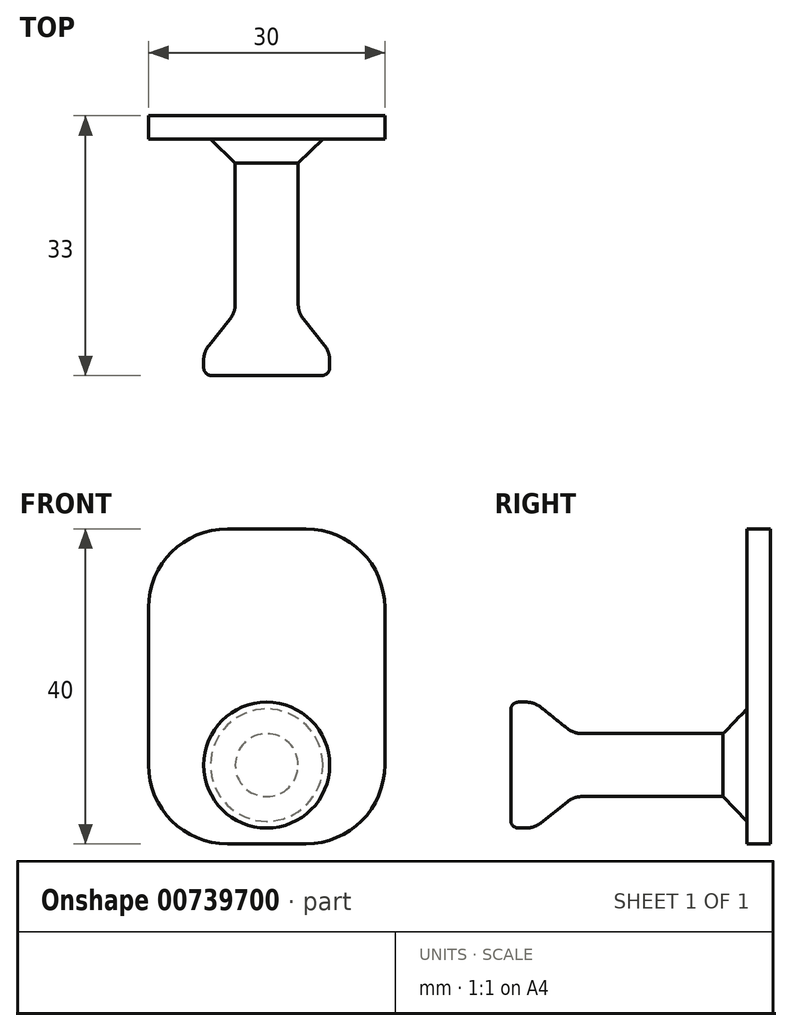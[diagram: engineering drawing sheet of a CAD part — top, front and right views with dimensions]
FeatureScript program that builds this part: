
annotation { "Feature Type Name" : "Feature", "Feature Type Description" : "" }
export const myFeature = defineFeature(function(context is Context, id is Id, definition is map)
    precondition{}
    {
        {
            var Q0;
            Q0=qCreatedBy(makeId("Front.planeOp"),FACE);
            var sketch = newSketch(context, id + "F0", { "sketchPlane" : qUnion([Q0])});
            skLineSegment(sketch, "E0.bottom", {"start": v(-5, 20) * mm, "end": v(5, 20) * mm});
            skLineSegment(sketch, "E0.top", {"start": v(-5, -20) * mm, "end": v(5, -20) * mm});
            skLineSegment(sketch, "E0.left", {"start": v(-15, 10) * mm, "end": v(-15, -10) * mm});
            skLineSegment(sketch, "E0.right", {"start": v(15, 10) * mm, "end": v(15, -10) * mm});
            skPoint(sketch, "E1.visualSharp", {"position": v(-15, 20) * mm});
            skArc(sketch, "E1.filletArc", {"start": v(-5, 20) * mm, "mid": v(-12.07, 17.07) * mm, "end": v(-15, 10) * mm});
            skPoint(sketch, "E2.visualSharp", {"position": v(15, 20) * mm});
            skArc(sketch, "E2.filletArc", {"start": v(15, 10) * mm, "mid": v(12.07, 17.07) * mm, "end": v(5, 20) * mm});
            skPoint(sketch, "E3.visualSharp", {"position": v(15, -20) * mm});
            skArc(sketch, "E3.filletArc", {"start": v(5, -20) * mm, "mid": v(12.07, -17.07) * mm, "end": v(15, -10) * mm});
            skPoint(sketch, "E4.visualSharp", {"position": v(-15, -20) * mm});
            skArc(sketch, "E4.filletArc", {"start": v(-15, -10) * mm, "mid": v(-12.07, -17.07) * mm, "end": v(-5, -20) * mm});
            skSolve(sketch);
        }
        {
            var Q0;
            Q0=makeQuery(id+"F0.imprint","IMPRINT",FACE,{"disambiguationData":[TD([[makeQuery(id+"F0.imprint","IMPRINT",EDGE,{"derivedFrom":sQuery(id+"F0.wireOp",EDGE,"E0.bottom")}),-1.0]])]});
            extrude(context, id + "F1", {"entities" : qUnion([Q0]), "depth" : 3 * mm, "offsetDistance" : 25 * mm});
        }
        {
            var Q0;
            Q0=makeQuery(id+"F1.opExtrude","CAP_FACE",FACE,{"disambiguationData":[OSD([sQuery(id+"F0.wireOp",EDGE,"E0.bottom"),sQuery(id+"F0.wireOp",EDGE,"E0.top"),sQuery(id+"F0.wireOp",EDGE,"E0.left"),sQuery(id+"F0.wireOp",EDGE,"E0.right"),sQuery(id+"F0.wireOp",EDGE,"E1.filletArc"),sQuery(id+"F0.wireOp",EDGE,"E2.filletArc"),sQuery(id+"F0.wireOp",EDGE,"E3.filletArc"),sQuery(id+"F0.wireOp",EDGE,"E4.filletArc")])],"isStart":false});
            var sketch = newSketch(context, id + "F2", { "sketchPlane" : qUnion([Q0])});
            skLineSegment(sketch, "E5", {"start": v(15, -10) * mm, "end": v(-15, -10) * mm, "construction": true});
            skLineSegment(sketch, "E6", {"start": v(0, -20) * mm, "end": v(0, -10) * mm, "construction": true});
            skCircle(sketch, "E7", {"center": v(0, -10) * mm, "radius": 5 * mm});
            skSolve(sketch);
        }
        {
            var Q0;
            Q0=makeQuery(id+"F1.opExtrude","SWEPT_FACE",FACE,{"disambiguationData":[OSD([sQuery(id+"F0.wireOp",EDGE,"E0.right")])]});
            cPlane(context, id + "F3", {"entities" : qUnion([Q0]), "cplaneType" : CPlaneType.OFFSET, "offset" : 15 * mm, "oppositeDirection" : true, "width" : 150 * mm, "height" : 150 * mm});
        }
        {
            var Q0;
            Q0=qCreatedBy(id+"F3.planeOp",FACE);
            var sketch = newSketch(context, id + "F4", { "sketchPlane" : qUnion([Q0])});
            skPoint(sketch, "E8.0", {"position": v(-3, -10) * mm});
            skLineSegment(sketch, "E9", {"start": v(-3, -10) * mm, "end": v(-33, -10) * mm});
            skLineSegment(sketch, "E10", {"start": v(-33, -10) * mm, "end": v(-33, -3) * mm});
            skLineSegment(sketch, "E11", {"start": v(-32, -2) * mm, "end": v(-31.05, -2) * mm});
            skLineSegment(sketch, "E12", {"start": v(-29.18, -2.66) * mm, "end": v(-25.82, -5.34) * mm});
            skLineSegment(sketch, "E13", {"start": v(-23.95, -6) * mm, "end": v(-6.02, -6) * mm});
            skLineSegment(sketch, "E14", {"start": v(-3, -6) * mm, "end": v(-3, -10) * mm});
            skLineSegment(sketch, "E15", {"start": v(-3, -10) * mm, "end": v(-46.2, -10) * mm, "construction": true});
            skPoint(sketch, "E16.visualSharp", {"position": v(-33, -2) * mm});
            skArc(sketch, "E16.filletArc", {"start": v(-32, -2) * mm, "mid": v(-32.7, -2.3) * mm, "end": v(-33, -3) * mm});
            skPoint(sketch, "E17.visualSharp", {"position": v(-30, -2) * mm});
            skArc(sketch, "E17.filletArc", {"start": v(-29.18, -2.66) * mm, "mid": v(-30.06, -2.17) * mm, "end": v(-31.05, -2) * mm});
            skPoint(sketch, "E18.visualSharp", {"position": v(-25, -6) * mm});
            skArc(sketch, "E18.filletArc", {"start": v(-25.82, -5.34) * mm, "mid": v(-24.94, -5.83) * mm, "end": v(-23.95, -6) * mm});
            skLineSegment(sketch, "E19", {"start": v(-6.02, -6) * mm, "end": v(-3, -2.87) * mm});
            skLineSegment(sketch, "E20", {"start": v(-3, -2.87) * mm, "end": v(-3, -6) * mm});
            skSolve(sketch);
        }
        {
            var Q0;
            Q0=makeQuery(id+"F4.imprint","IMPRINT",FACE,{"disambiguationData":[TD([[makeQuery(id+"F4.imprint","IMPRINT",EDGE,{"derivedFrom":sQuery(id+"F4.wireOp",EDGE,"E9")}),-1.0]])]});
            var Q1;
            Q1=sQuery(id+"F4.wireOp",EDGE,"E15");
            revolve(context, id + "F5", {"operationType" : NewBodyOperationType.ADD, "surfaceOperationType" : NewSurfaceOperationType.NEW, "entities" : qUnion([Q0]), "axis" : qUnion([Q1]), "revolveType" : RevolveType.FULL});
        }
    });
